# Revit family: KM1.00
name_source: partatom
category: Plumbing Fixtures
revit_build: Autodesk Revit Architecture 2012 (Build: 20110309_2315(x64)
units: mm (PartAtom-declared; Revit-internal decimal feet)

## types (1)
- KM1.00
    Assembly Code = D2010
    CW Connection = Yes
    CWFU = 0
    Captive linkage = C-FJ8.24
    Cost = 0 $
    Default Elevation = 0' - 0"
    Description = Exposed with integral Ball-O-Stop. Non-hold open. 3/4" FI
    HW Connection = No
    HWFU = 0
    Keynote = Mainly used for industrial/institutional shower installations. (Also used for wash    basin outlets.)
    Knee /elbow lever = C-KM9.12/19
    Manufacturer = COBRA
    Material = Chrome - Brushed
    Metering chain ass. = C-KM9.11
    Model = KM1.00
    Piston assembly (Applicable for urinal diaphragm) = C-FJ8.11
    Range = Metering Valves
    Top cover = C-FJC1.2
    Type Comments = SANS 1808-9
    URL = http://www.cobra.co.za
    Vent Connection = No
    WFU = 0
    Waste Connection = No

## geometry (parser evidence)
native form markers: Blend x4
no freeform markers — native parametric forms only
